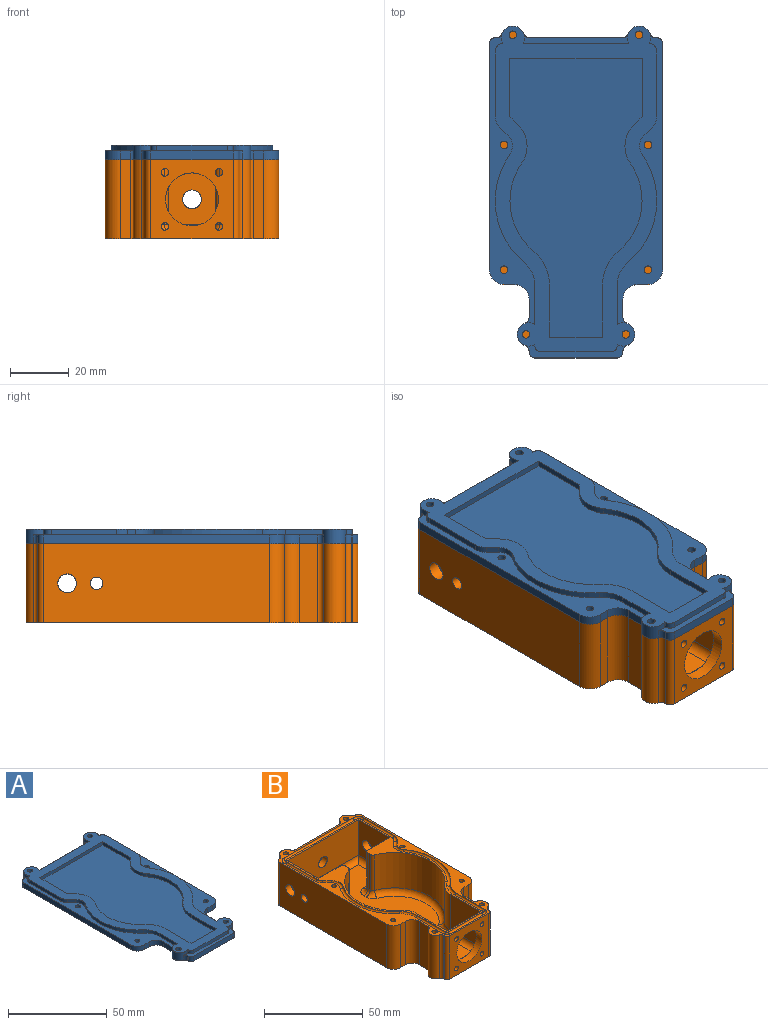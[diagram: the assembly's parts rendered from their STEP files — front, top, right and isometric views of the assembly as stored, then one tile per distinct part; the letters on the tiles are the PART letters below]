
ASSEMBLY  parts=2 mates=1
PART A: 85 faces, bbox 59x113x5 mm
  f0: plane 36.07x3.33mm, normal (0,0,1), area 71.6mm2, adj f3,f36,f37,f38,f39,f40
  f1: plane 98.87x15.5mm, normal (0,0,1), area 414.3mm2, adj f2,f8,f26,f27,f28,f29,f30,f31
  f2: plane 2x0.04mm, normal (0,1,0), area 0.1mm2, adj f1,f36,f44,f61
  f3: plane 36.07x2mm, normal (0,1,0), area 72.1mm2, adj f0,f36,f40,f44
  f4: plane 98.87x15.5mm, normal (0,0,1), area 414.3mm2, adj f5,f9,f11,f12,f13,f14,f15,f16
  f5: plane 2x0.04mm, normal (0,1,0), area 0.1mm2, adj f4,f40,f44,f45
  f6: plane 34.67x4.54mm, normal (0,0,1), area 73.6mm2, adj f7,f10,f18,f19,f20,f21,f22,f23
  f7: plane 2x0.54mm, normal (1,0,0), area 1.1mm2, adj f6,f26,f44,f54
  f8: plane 13.22x2mm, normal (1,0,0), area 26.4mm2, adj f1,f26,f44,f55
  f9: plane 13.22x2mm, normal (-1,0,0), area 26.4mm2, adj f4,f18,f44,f51
  f10: plane 2x0.54mm, normal (-1,0,0), area 1.1mm2, adj f6,f18,f44,f52
  f11: cylinder r=2mm len=3mm, axis (0,0,-1), area 9.4mm2, adj f4,f12,f42,f43
  f12: plane 77x3mm, normal (-1,0,0), area 231mm2, adj f4,f11,f13,f43
  f13: cylinder r=5mm len=5mm, axis (0,0,-1), area 23.6mm2, adj f4,f12,f14,f43
  f14: plane 3.5x3mm, normal (0,-1,0), area 10.5mm2, adj f4,f13,f15,f43
  f15: cylinder r=5mm len=5mm, axis (0,0,-1), area 23.6mm2, adj f4,f14,f16,f43
  f16: plane 6.34x3mm, normal (-1,0,0), area 19mm2, adj f4,f15,f17,f43
  f17: cylinder r=2mm len=3mm, axis (0,0,-1), area 7.4mm2, adj f4,f16,f18,f43
  f18: cylinder r=4mm len=8mm, axis (0,0,-1), area 63.1mm2, adj f4,f6,f9,f10,f17,f19,f43,f44
  f19: cylinder r=2mm len=3mm, axis (0,0,-1), area 7.4mm2, adj f6,f18,f20,f43
  f20: plane 3x0.34mm, normal (-1,0,0), area 1mm2, adj f6,f19,f21,f43
  f21: cylinder r=2mm len=3mm, axis (0,0,-1), area 9.4mm2, adj f6,f20,f22,f43
  f22: plane 28x3mm, normal (0,-1,0), area 84mm2, adj f6,f21,f23,f43
  f23: cylinder r=2mm len=3mm, axis (0,0,-1), area 9.4mm2, adj f6,f22,f24,f43
  f24: plane 3x0.34mm, normal (1,0,0), area 1mm2, adj f6,f23,f25,f43
  f25: cylinder r=2mm len=3mm, axis (0,0,-1), area 7.4mm2, adj f6,f24,f26,f43
  f26: cylinder r=4mm len=8mm, axis (0,0,-1), area 63.1mm2, adj f1,f6,f7,f8,f25,f27,f43,f44
  f27: cylinder r=2mm len=3mm, axis (0,0,-1), area 7.4mm2, adj f1,f26,f28,f43
  f28: plane 6.34x3mm, normal (1,0,0), area 19mm2, adj f1,f27,f29,f43
  f29: cylinder r=5mm len=5mm, axis (0,0,-1), area 23.6mm2, adj f1,f28,f30,f43
  f30: plane 3.5x3mm, normal (0,-1,0), area 10.5mm2, adj f1,f29,f31,f43
  f31: cylinder r=5mm len=5mm, axis (0,0,-1), area 23.6mm2, adj f1,f30,f32,f43
  f32: plane 77x3mm, normal (1,0,0), area 231mm2, adj f1,f31,f33,f43
  f33: cylinder r=2mm len=3mm, axis (0,0,-1), area 9.4mm2, adj f1,f32,f34,f43
  f34: plane 3x0.34mm, normal (0,1,0), area 1mm2, adj f1,f33,f35,f43
  f35: cylinder r=2mm len=3mm, axis (0,0,-1), area 7.4mm2, adj f1,f34,f36,f43
  f36: cylinder r=4mm len=8mm, axis (0,0,-1), area 63.1mm2, adj f0,f1,f2,f3,f35,f37,f43,f44
  f37: cylinder r=2mm len=3mm, axis (0,0,-1), area 7.4mm2, adj f0,f36,f38,f43
  f38: plane 31.69x3mm, normal (0,1,0), area 95.1mm2, adj f0,f37,f39,f43
  f39: cylinder r=2mm len=3mm, axis (0,0,-1), area 7.4mm2, adj f0,f38,f40,f43
  f40: cylinder r=4mm len=8mm, axis (0,0,-1), area 63.1mm2, adj f0,f3,f4,f5,f39,f41,f43,f44
  f41: cylinder r=2mm len=3mm, axis (0,0,-1), area 7.4mm2, adj f4,f40,f42,f43
  f42: plane 3x0.34mm, normal (0,1,0), area 1mm2, adj f4,f11,f41,f43
  f43: plane 113x59mm, normal (0,0,-1), area 5814.4mm2, adj f11,f12,f13,f14,f15,f16,f17,f18
  f44: plane 111x55mm, normal (0,0,1), area 1573.5mm2, adj f2,f3,f5,f7,f8,f9,f10,f18
  f45: cylinder r=2.5mm len=2.5mm, axis (0,0,1), area 7.9mm2, adj f4,f5,f44,f46
  f46: plane 22.43x2mm, normal (-1,0,0), area 44.9mm2, adj f4,f44,f45,f47
  f47: cylinder r=5mm len=3.54mm, axis (0,0,1), area 7.9mm2, adj f4,f44,f46,f48
  f48: plane 2.91x2.91mm, normal (-0.71,-0.71,0), area 8.2mm2, adj f4,f44,f47,f49
  f49: cylinder r=5mm len=6.4mm, axis (0,0,1), area 13.9mm2, adj f4,f44,f48,f50
  f50: cylinder r=27.5mm len=36.86mm, axis (0,0,1), area 81.7mm2, adj f4,f44,f49,f51
  f51: cylinder r=10mm len=7.68mm, axis (0,0,1), area 17.5mm2, adj f4,f9,f44,f50
  f52: cylinder r=2mm len=2mm, axis (0,0,1), area 6.3mm2, adj f6,f10,f44,f53
  f53: plane 24x2mm, normal (0,-1,0), area 48mm2, adj f6,f44,f52,f54
  f54: cylinder r=2mm len=2mm, axis (0,0,1), area 6.3mm2, adj f6,f7,f44,f53
  f55: cylinder r=10mm len=7.68mm, axis (0,0,1), area 17.5mm2, adj f1,f8,f44,f56
  f56: cylinder r=27.5mm len=36.86mm, axis (0,0,1), area 81.7mm2, adj f1,f44,f55,f57
  f57: cylinder r=5mm len=6.4mm, axis (0,0,1), area 13.9mm2, adj f1,f44,f56,f58
  f58: plane 2.91x2.91mm, normal (0.71,-0.71,0), area 8.2mm2, adj f1,f44,f57,f59
  f59: cylinder r=5mm len=3.54mm, axis (0,0,1), area 7.9mm2, adj f1,f44,f58,f60
  f60: plane 22.43x2mm, normal (1,0,0), area 44.9mm2, adj f1,f44,f59,f61
  f61: cylinder r=2.5mm len=2.5mm, axis (0,0,1), area 7.9mm2, adj f1,f2,f44,f60
  f62: plane 45x2mm, normal (0,-1,0), area 90mm2, adj f44,f63,f75,f76
  f63: plane 19.93x2mm, normal (1,0,0), area 39.9mm2, adj f44,f62,f64,f76
  f64: plane 2.91x2.91mm, normal (0.71,0.71,0), area 8.2mm2, adj f44,f63,f65,f76
  f65: cylinder r=10mm len=12.79mm, axis (0,0,1), area 27.9mm2, adj f44,f64,f66,f76
  f66: cylinder r=22.5mm len=30.16mm, axis (0,0,1), area 66.8mm2, adj f44,f65,f67,f76
  f67: cylinder r=15mm len=11.53mm, axis (0,0,1), area 26.3mm2, adj f44,f66,f68,f76
  f68: plane 17.69x2mm, normal (1,0,0), area 35.4mm2, adj f44,f67,f69,f76
  f69: plane 18x2mm, normal (0,1,0), area 36mm2, adj f44,f68,f70,f76
  f70: plane 17.69x2mm, normal (-1,0,0), area 35.4mm2, adj f44,f69,f71,f76
  f71: cylinder r=15mm len=11.53mm, axis (0,0,1), area 26.3mm2, adj f44,f70,f72,f76
  f72: cylinder r=22.5mm len=30.16mm, axis (0,0,1), area 66.8mm2, adj f44,f71,f73,f76
  f73: cylinder r=10mm len=12.79mm, axis (0,0,1), area 27.9mm2, adj f44,f72,f74,f76
  f74: plane 2.91x2.91mm, normal (-0.71,0.71,0), area 8.2mm2, adj f44,f73,f75,f76
  f75: plane 19.93x2mm, normal (-1,0,0), area 39.9mm2, adj f44,f62,f74,f76
  f76: plane 95x45mm, normal (0,0,1), area 3267.1mm2, adj f62,f63,f64,f65,f66,f67,f68,f69
  f77: cylinder r=1.3mm len=5mm, axis (0,0,1), area 40.8mm2, adj f43,f44
  f78: cylinder r=1.3mm len=5mm, axis (0,0,1), area 40.8mm2, adj f43,f44
  f79: cylinder r=1.3mm len=5mm, axis (0,0,1), area 40.8mm2, adj f43,f44
  f80: cylinder r=1.3mm len=5mm, axis (0,0,1), area 40.8mm2, adj f43,f44
  f81: cylinder r=1.3mm len=3mm, axis (0,0,1), area 24.5mm2, adj f1,f43
  f82: cylinder r=1.3mm len=3mm, axis (0,0,1), area 24.5mm2, adj f4,f43
  f83: cylinder r=1.3mm len=3mm, axis (0,0,1), area 24.5mm2, adj f1,f43
  f84: cylinder r=1.3mm len=3mm, axis (0,0,1), area 24.5mm2, adj f4,f43
PART B: 118 faces, bbox 61.7x113x27.5 mm
  f0: plane 113x59mm, normal (0,0,1), area 824.2mm2, adj f2,f3,f4,f5,f6,f7,f8,f9
  f1: plane 103.04x53.04mm, normal (0,0,1), area 538.9mm2, adj f35,f36,f37,f38,f39,f40,f41,f42
  f2: cylinder r=2mm len=27mm, axis (0,0,-1), area 84.8mm2, adj f0,f3,f33,f34
  f3: plane 77x27mm, normal (-1,0,0), area 2032.3mm2, adj f0,f2,f4,f34,f77,f78
  f4: cylinder r=5mm len=27mm, axis (0,0,-1), area 212.1mm2, adj f0,f3,f5,f34
  f5: plane 27x3.5mm, normal (0,-1,0), area 94.5mm2, adj f0,f4,f6,f34
  f6: cylinder r=5mm len=27mm, axis (0,0,-1), area 212.1mm2, adj f0,f5,f7,f34
  f7: plane 27x6.34mm, normal (-1,0,0), area 171.3mm2, adj f0,f6,f8,f34
  f8: cylinder r=2mm len=27mm, axis (0,0,-1), area 66.5mm2, adj f0,f7,f9,f34
  f9: cylinder r=4mm len=27mm, axis (0,0,-1), area 265.9mm2, adj f0,f8,f10,f34
  f10: cylinder r=2mm len=27mm, axis (0,0,-1), area 66.5mm2, adj f0,f9,f11,f34
  f11: plane 27x0.34mm, normal (-1,0,0), area 9.3mm2, adj f0,f10,f12,f34
  f12: cylinder r=2mm len=27mm, axis (0,0,-1), area 84.8mm2, adj f0,f11,f13,f34
  f13: plane 28x27mm, normal (0,-1,0), area 480.3mm2, adj f0,f12,f14,f34,f72,f73,f74,f75
  f14: cylinder r=2mm len=27mm, axis (0,0,-1), area 84.8mm2, adj f0,f13,f15,f34
  f15: plane 27x0.34mm, normal (1,0,0), area 9.3mm2, adj f0,f14,f16,f34
  f16: cylinder r=2mm len=27mm, axis (0,0,-1), area 66.5mm2, adj f0,f15,f17,f34
  f17: cylinder r=4mm len=27mm, axis (0,0,-1), area 265.9mm2, adj f0,f16,f18,f34
  f18: cylinder r=2mm len=27mm, axis (0,0,-1), area 66.5mm2, adj f0,f17,f19,f34
  f19: plane 27x6.34mm, normal (1,0,0), area 171.3mm2, adj f0,f18,f20,f34
  f20: cylinder r=5mm len=27mm, axis (0,0,-1), area 212.1mm2, adj f0,f19,f21,f34
  f21: plane 27x3.5mm, normal (0,-1,0), area 94.5mm2, adj f0,f20,f22,f34
  f22: cylinder r=5mm len=27mm, axis (0,0,-1), area 212.1mm2, adj f0,f21,f23,f34
  f23: plane 77x27mm, normal (1,0,0), area 2032.3mm2, adj f0,f22,f24,f34,f79,f80
  f24: cylinder r=2mm len=27mm, axis (0,0,-1), area 84.8mm2, adj f0,f23,f25,f34
  f25: plane 27x0.34mm, normal (0,1,0), area 9.3mm2, adj f0,f24,f26,f34
  f26: cylinder r=2mm len=27mm, axis (0,0,-1), area 66.5mm2, adj f0,f25,f27,f34
  f27: cylinder r=4mm len=27mm, axis (0,0,-1), area 265.9mm2, adj f0,f26,f28,f34
  f28: cylinder r=2mm len=27mm, axis (0,0,-1), area 66.5mm2, adj f0,f27,f29,f34
  f29: plane 31.69x27mm, normal (0,1,0), area 823.4mm2, adj f0,f28,f30,f34,f101
  f30: cylinder r=2mm len=27mm, axis (0,0,-1), area 66.5mm2, adj f0,f29,f31,f34
  f31: cylinder r=4mm len=27mm, axis (0,0,-1), area 265.9mm2, adj f0,f30,f32,f34
  f32: cylinder r=2mm len=27mm, axis (0,0,-1), area 66.5mm2, adj f0,f31,f33,f34
  f33: plane 27x0.34mm, normal (0,1,0), area 9.3mm2, adj f0,f2,f32,f34
  f34: plane 113x59mm, normal (0,0,-1), area 5856.9mm2, adj f2,f3,f4,f5,f6,f7,f8,f9
  f35: cylinder r=2mm len=22mm, axis (0,0,1), area 69.1mm2, adj f1,f36,f52,f67
  f36: plane 22x1.6mm, normal (1,0,0), area 35.1mm2, adj f1,f35,f37,f65
  f37: cylinder r=2mm len=22mm, axis (0,0,1), area 52.7mm2, adj f1,f36,f38,f63
  f38: cylinder r=25.5mm len=43.77mm, axis (0,0,1), area 1178.7mm2, adj f1,f37,f39,f61
  f39: cylinder r=10mm len=22mm, axis (0,0,1), area 198.5mm2, adj f1,f38,f40,f59
  f40: plane 22x21.64mm, normal (1,0,0), area 476.1mm2, adj f1,f39,f41,f57
  f41: plane 24x22mm, normal (0,1,0), area 263mm2, adj f1,f40,f42,f55,f72,f73,f74,f75
  f42: plane 22x21.64mm, normal (-1,0,0), area 476.1mm2, adj f1,f41,f43,f54
  f43: cylinder r=10mm len=22mm, axis (0,0,1), area 198.5mm2, adj f1,f42,f44,f56
  f44: cylinder r=25.5mm len=43.77mm, axis (0,0,1), area 1178.7mm2, adj f1,f43,f45,f58
  f45: cylinder r=2mm len=22mm, axis (0,0,1), area 52.7mm2, adj f1,f44,f46,f60
  f46: plane 22x1.6mm, normal (-1,0,0), area 35.1mm2, adj f1,f45,f47,f62
  f47: cylinder r=2mm len=22mm, axis (0,0,1), area 69.1mm2, adj f1,f46,f48,f64
  f48: plane 22x15.5mm, normal (0,1,0), area 341mm2, adj f1,f47,f49,f66
  f49: plane 22.29x22mm, normal (-1,0,0), area 443.6mm2, adj f1,f48,f50,f68,f79,f80
  f50: plane 51x22mm, normal (0,-1,0), area 1089.8mm2, adj f1,f49,f51,f70,f101
  f51: plane 22.29x22mm, normal (1,0,0), area 443.6mm2, adj f1,f50,f52,f71,f77,f78
  f52: plane 22x15.5mm, normal (0,1,0), area 341mm2, adj f1,f35,f51,f69
  f53: plane 95x45mm, normal (0,0,1), area 2895.4mm2, adj f54,f55,f56,f57,f58,f59,f60,f61
  f54: cylinder r=3mm len=21.64mm, axis (0,1,0), area 96.8mm2, adj f42,f53,f55,f56
  f55: cylinder r=3mm len=24mm, axis (1,0,0), area 91.5mm2, adj f41,f53,f54,f57,f72,f73,f74
  f56: torus R=13mm, axis (0,0,1), area 47.2mm2, adj f43,f53,f54,f58
  f57: cylinder r=3mm len=21.64mm, axis (0,-1,0), area 96.8mm2, adj f40,f53,f55,f59
  f58: torus R=22.5mm, axis (0,0,1), area 241.7mm2, adj f44,f53,f56,f60
  f59: torus R=13mm, axis (0,0,1), area 47.2mm2, adj f39,f53,f57,f61
  f60: torus R=5mm, axis (0,0,1), area 17.5mm2, adj f45,f53,f58,f62
  f61: torus R=22.5mm, axis (0,0,1), area 241.7mm2, adj f38,f53,f59,f63
  f62: cylinder r=3mm len=3mm, axis (0,1,0), area 7.5mm2, adj f46,f53,f60,f64
  f63: torus R=5mm, axis (0,0,1), area 17.5mm2, adj f37,f53,f61,f65
  f64: torus R=5mm, axis (0,0,1), area 22.9mm2, adj f47,f53,f62,f66
  f65: cylinder r=3mm len=3mm, axis (0,-1,0), area 7.5mm2, adj f36,f53,f63,f67
  f66: cylinder r=3mm len=15.5mm, axis (1,0,0), area 67.9mm2, adj f48,f53,f64,f68
  f67: torus R=5mm, axis (0,0,1), area 22.9mm2, adj f35,f53,f65,f69
  f68: cylinder r=3mm len=22.29mm, axis (0,1,0), area 94.8mm2, adj f49,f53,f66,f70
  f69: cylinder r=3mm len=15.5mm, axis (1,0,0), area 67.9mm2, adj f52,f53,f67,f71
  f70: cylinder r=3mm len=51mm, axis (-1,0,0), area 230.1mm2, adj f50,f53,f68,f71
  f71: cylinder r=3mm len=22.29mm, axis (0,-1,0), area 94.8mm2, adj f51,f53,f69,f70
  f72: cylinder r=1.3mm len=4.76mm, axis (0,-1,0), area 34.6mm2, adj f13,f41,f55
  f73: cylinder r=9mm len=18mm, axis (0,-1,0), area 226.3mm2, adj f13,f41,f55
  f74: cylinder r=1.3mm len=4.76mm, axis (0,-1,0), area 34.6mm2, adj f13,f41,f55
  f75: cylinder r=1.3mm len=4mm, axis (0,-1,0), area 32.7mm2, adj f13,f41
  f76: cylinder r=1.3mm len=4mm, axis (0,-1,0), area 32.7mm2, adj f13,f41
  f77: cylinder r=2.15mm len=4.3mm, axis (-1,0,0), area 54mm2, adj f3,f51
  f78: cylinder r=3.2mm len=6.4mm, axis (-1,0,0), area 80.4mm2, adj f3,f51
  f79: cylinder r=2.15mm len=4.3mm, axis (-1,0,0), area 54mm2, adj f23,f49
  f80: cylinder r=3.2mm len=6.4mm, axis (-1,0,0), area 80.4mm2, adj f23,f49
  f81: torus R=5mm, axis (0,0,-1), area 25mm2, adj f0,f1,f82,f100
  f82: cylinder r=1mm len=4.62mm, axis (0.71,-0.71,0), area 16.1mm2, adj f0,f1,f81,f83
  f83: torus R=5mm, axis (0,0,1), area 13.9mm2, adj f0,f1,f82,f84
  f84: cylinder r=1mm len=21.72mm, axis (0,-1,0), area 77mm2, adj f0,f1,f83,f85
  f85: torus R=2.5mm, axis (0,0,1), area 13.9mm2, adj f0,f1,f84,f86
  f86: cylinder r=1mm len=50mm, axis (-1,0,0), area 177.2mm2, adj f0,f1,f85,f87
  f87: torus R=2.5mm, axis (0,0,1), area 13.9mm2, adj f0,f1,f86,f88
  f88: cylinder r=1mm len=21.72mm, axis (0,1,0), area 77mm2, adj f0,f1,f87,f89
  f89: torus R=5mm, axis (0,0,1), area 13.9mm2, adj f0,f1,f88,f90
  f90: cylinder r=1mm len=4.62mm, axis (0.71,0.71,0), area 16.1mm2, adj f0,f1,f89,f91
  f91: torus R=5mm, axis (0,0,-1), area 25mm2, adj f0,f1,f90,f92
  f92: torus R=27.5mm, axis (0,0,1), area 146.3mm2, adj f0,f1,f91,f93
  f93: torus R=10mm, axis (0,0,-1), area 31.1mm2, adj f0,f1,f92,f94
  f94: cylinder r=1mm len=20.69mm, axis (0,1,0), area 73.3mm2, adj f0,f1,f93,f95
  f95: torus R=2mm, axis (0,0,1), area 11.1mm2, adj f0,f1,f94,f96
  f96: cylinder r=1mm len=24mm, axis (1,0,0), area 85.1mm2, adj f0,f1,f95,f97
  f97: torus R=2mm, axis (0,0,1), area 11.1mm2, adj f0,f1,f96,f98
  f98: cylinder r=1mm len=20.69mm, axis (0,-1,0), area 73.3mm2, adj f0,f1,f97,f99
  f99: torus R=10mm, axis (0,0,-1), area 31.1mm2, adj f0,f1,f98,f100
  f100: torus R=27.5mm, axis (0,0,1), area 146.3mm2, adj f0,f1,f81,f99
  f101: cylinder r=3.2mm len=6.4mm, axis (0,1,0), area 80.4mm2, adj f29,f50
  f102: cylinder r=1.3mm len=20mm, axis (0,0,1), area 163.4mm2, adj f0,f103
  f103: plane 2.6x2.6mm, normal (0,0,1), area 5.3mm2, adj f102
  f104: cylinder r=1.3mm len=20mm, axis (0,0,1), area 163.4mm2, adj f0,f105
  f105: plane 2.6x2.6mm, normal (0,0,1), area 5.3mm2, adj f104
  f106: cylinder r=1.3mm len=20mm, axis (0,0,1), area 163.4mm2, adj f0,f107
  f107: plane 2.6x2.6mm, normal (0,0,1), area 5.3mm2, adj f106
  f108: cylinder r=1.3mm len=20mm, axis (0,0,1), area 163.4mm2, adj f0,f109
  f109: plane 2.6x2.6mm, normal (0,0,1), area 5.3mm2, adj f108
  f110: cylinder r=1.3mm len=20mm, axis (0,0,1), area 163.4mm2, adj f0,f111
  f111: plane 2.6x2.6mm, normal (0,0,1), area 5.3mm2, adj f110
  f112: cylinder r=1.3mm len=20mm, axis (0,0,1), area 163.4mm2, adj f0,f113
  f113: plane 2.6x2.6mm, normal (0,0,1), area 5.3mm2, adj f112
  f114: cylinder r=1.3mm len=20mm, axis (0,0,1), area 163.4mm2, adj f0,f115
  f115: plane 2.6x2.6mm, normal (0,0,1), area 5.3mm2, adj f114
  f116: cylinder r=1.3mm len=20mm, axis (0,0,1), area 163.4mm2, adj f0,f117
  f117: plane 2.6x2.6mm, normal (0,0,1), area 5.3mm2, adj f116
PLACE A t=(-29.64,-19.83,12.04)mm
PLACE B t=(-29.64,-19.83,-14.96)mm
MATE parallel A.f13 <-> B.f4  axis (0,0,-1) through (-54.14,-43.33,12.04)mm
